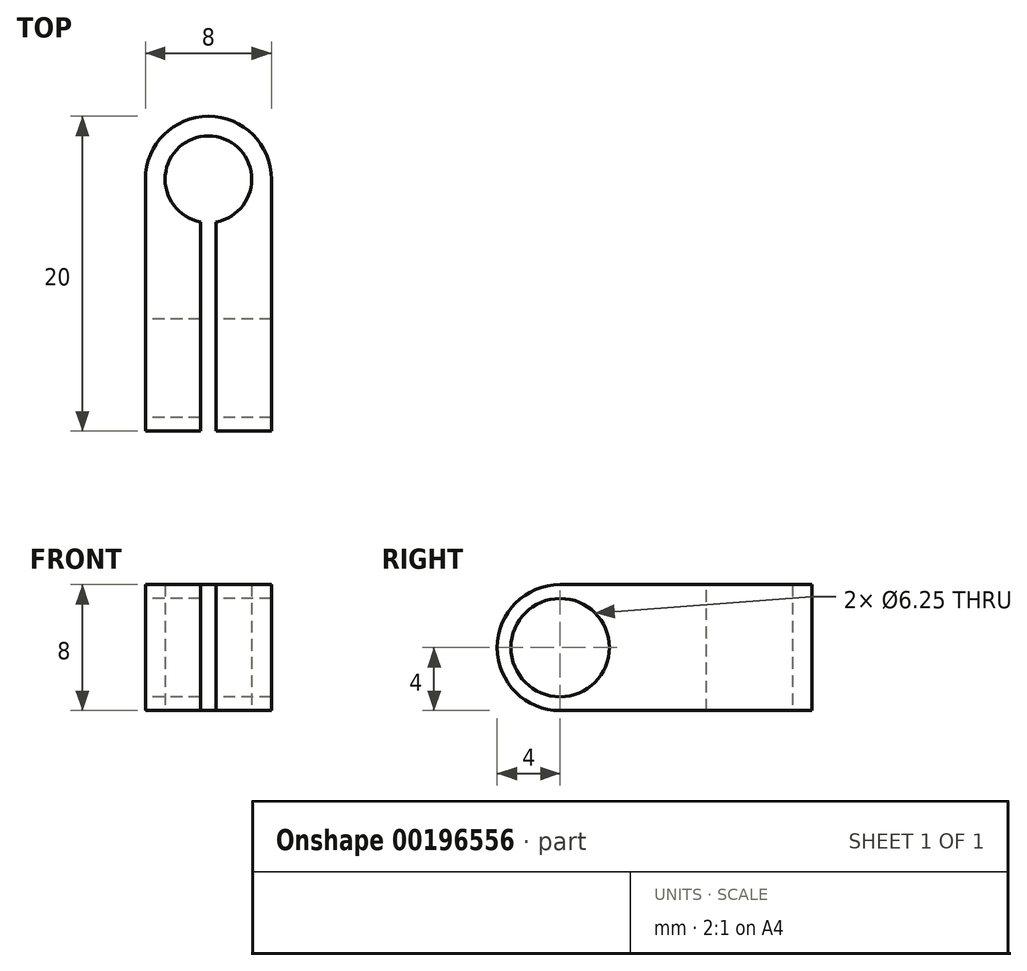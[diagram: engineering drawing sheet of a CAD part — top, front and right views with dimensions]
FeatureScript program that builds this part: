
annotation { "Feature Type Name" : "Feature", "Feature Type Description" : "" }
export const myFeature = defineFeature(function(context is Context, id is Id, definition is map)
    precondition{}
    {
        {
            var Q0;
            Q0=qCreatedBy(makeId("Front.planeOp"),FACE);
            var sketch = newSketch(context, id + "F0", { "sketchPlane" : qUnion([Q0])});
            skLineSegment(sketch, "E0.bottom", {"start": v(0, 0) * mm, "end": v(8, 0) * mm});
            skLineSegment(sketch, "E0.top", {"start": v(0, 8) * mm, "end": v(8, 8) * mm});
            skLineSegment(sketch, "E0.left", {"start": v(0, 0) * mm, "end": v(0, 8) * mm});
            skLineSegment(sketch, "E0.right", {"start": v(8, 0) * mm, "end": v(8, 8) * mm});
            skSolve(sketch);
        }
        {
            var Q0;
            Q0=makeQuery(id+"F0.imprint","IMPRINT",FACE,{"disambiguationData":[TD([[makeQuery(id+"F0.imprint","IMPRINT",EDGE,{"derivedFrom":sQuery(id+"F0.wireOp",EDGE,"E0.bottom")}),1.0]])]});
            extrude(context, id + "F1", {"entities" : qUnion([Q0]), "depth" : 20 * mm});
        }
        {
            var Q0;
            Q0=makeQuery(id+"F1.opExtrude","CAP_FACE",FACE,{"disambiguationData":[OSD([sQuery(id+"F0.wireOp",EDGE,"E0.bottom"),sQuery(id+"F0.wireOp",EDGE,"E0.top"),sQuery(id+"F0.wireOp",EDGE,"E0.left"),sQuery(id+"F0.wireOp",EDGE,"E0.right")])],"isStart":false});
            var sketch = newSketch(context, id + "F2", { "sketchPlane" : qUnion([Q0])});
            skLineSegment(sketch, "E1", {"start": v(4, 8) * mm, "end": v(4.5, 8) * mm});
            skLineSegment(sketch, "E2", {"start": v(4.5, 8) * mm, "end": v(4.5, 0) * mm});
            skLineSegment(sketch, "E3", {"start": v(4.5, 0) * mm, "end": v(3.5, 0) * mm});
            skLineSegment(sketch, "E4", {"start": v(3.5, 0) * mm, "end": v(3.5, 8) * mm});
            skLineSegment(sketch, "E5", {"start": v(3.5, 8) * mm, "end": v(4, 8) * mm});
            skPoint(sketch, "E6.start.orphan", {"position": v(4, 0) * mm});
            skSolve(sketch);
        }
        {
            var Q0;
            Q0=makeQuery(id+"F2.imprint","IMPRINT",FACE,{"disambiguationData":[TD([[makeQuery(id+"F2.imprint","IMPRINT",EDGE,{"derivedFrom":sQuery(id+"F2.wireOp",EDGE,"E1")}),-1.0]])]});
            extrude(context, id + "F3", {"entities" : qUnion([Q0]), "operationType" : NewBodyOperationType.REMOVE, "oppositeDirection" : true, "depth" : 15 * mm});
        }
        {
            var Q0;
            Q0=makeQuery(id+"F1.opExtrude","CAP_EDGE",EDGE,{"disambiguationData":[OSD([sQuery(id+"F0.wireOp",EDGE,"E0.top")])],"isStart":false});
            var Q1;
            Q1=makeQuery(id+"F1.opExtrude","CAP_EDGE",EDGE,{"disambiguationData":[OSD([sQuery(id+"F0.wireOp",EDGE,"E0.bottom")])],"isStart":false});
            var Q2;
            Q2=makeQuery(id+"F1.opExtrude","CAP_EDGE",EDGE,{"disambiguationData":[OSD([sQuery(id+"F0.wireOp",EDGE,"E0.right")])],"isStart":true});
            var Q3;
            Q3=makeQuery(id+"F1.opExtrude","CAP_EDGE",EDGE,{"disambiguationData":[OSD([sQuery(id+"F0.wireOp",EDGE,"E0.left")])],"isStart":true});
            fillet(context, id + "F4", {"entities" : qUnion([Q0, Q1, Q2, Q3]), "radius" : 4 * mm, "tangentPropagation" : true, "allowEdgeOverflow" : false});
        }
        {
            var Q0;
            Q0=makeQuery(id+"F1.opExtrude","SWEPT_FACE",FACE,{"disambiguationData":[OSD([sQuery(id+"F0.wireOp",EDGE,"E0.top")])]});
            var sketch = newSketch(context, id + "F5", { "sketchPlane" : qUnion([Q0])});
            skCircle(sketch, "E7", {"center": v(4, -4) * mm, "radius": 2.75 * mm});
            skSolve(sketch);
        }
        {
            var Q0;
            Q0=makeQuery(id+"F5.imprint","IMPRINT",FACE,{"disambiguationData":[TD([[makeQuery(id+"F5.imprint","IMPRINT",EDGE,{"derivedFrom":sQuery(id+"F5.wireOp",EDGE,"E7")}),1.0]])]});
            extrude(context, id + "F6", {"entities" : qUnion([Q0]), "operationType" : NewBodyOperationType.ADD, "oppositeDirection" : true, "depth" : 10 * mm});
        }
        {
            var Q0;
            Q0=makeQuery(id+"F1.opExtrude","SWEPT_FACE",FACE,{"disambiguationData":[OSD([sQuery(id+"F0.wireOp",EDGE,"E0.right")])]});
            var sketch = newSketch(context, id + "F7", { "sketchPlane" : qUnion([Q0])});
            skCircle(sketch, "E8", {"center": v(-16, 4) * mm, "radius": 3.12 * mm});
            skSolve(sketch);
        }
        {
            var Q0;
            Q0=makeQuery(id+"F7.imprint","IMPRINT",FACE,{"disambiguationData":[TD([[makeQuery(id+"F7.imprint","IMPRINT",EDGE,{"derivedFrom":sQuery(id+"F7.wireOp",EDGE,"E8")}),1.0]])]});
            extrude(context, id + "F8", {"entities" : qUnion([Q0]), "operationType" : NewBodyOperationType.ADD, "endBound" : BoundingType.THROUGH_ALL, "oppositeDirection" : true, "depth" : 10 * mm});
        }
        {
            var Q0;
            Q0=makeQuery(id+"F6.opExtrude","CAP_FACE",FACE,{"disambiguationData":[OSD([sQuery(id+"F5.wireOp",EDGE,"E7")])],"isStart":false});
            extrude(context, id + "F9", {"entities" : qUnion([Q0]), "operationType" : NewBodyOperationType.REMOVE, "oppositeDirection" : true, "depth" : 25 * mm});
        }
        {
            var Q0;
            Q0=makeQuery(id+"F8.opExtrude","CAP_FACE",FACE,{"disambiguationData":[OSD([sQuery(id+"F7.wireOp",EDGE,"E8")])],"isStart":false});
            extrude(context, id + "F10", {"entities" : qUnion([Q0]), "operationType" : NewBodyOperationType.REMOVE, "oppositeDirection" : true, "depth" : 27 * mm});
        }
    });
